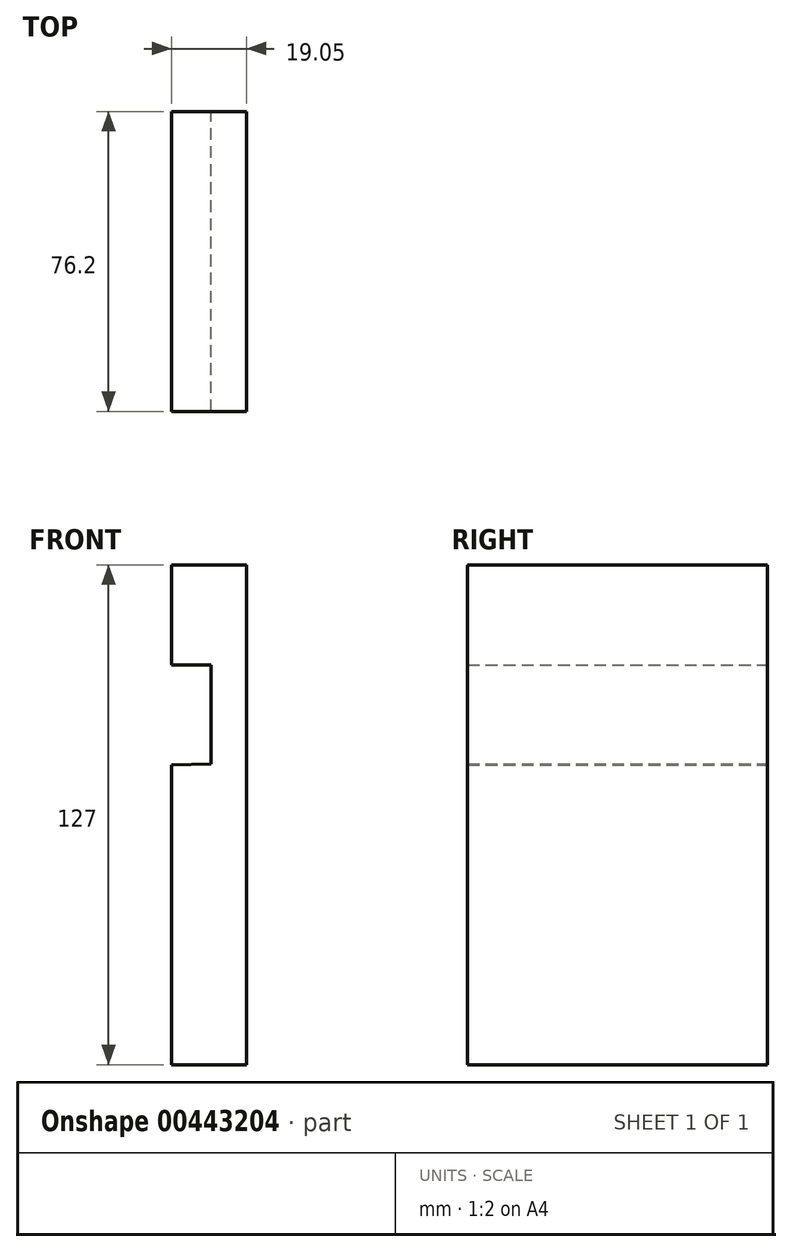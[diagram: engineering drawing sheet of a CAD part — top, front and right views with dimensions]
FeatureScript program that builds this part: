
annotation { "Feature Type Name" : "Feature", "Feature Type Description" : "" }
export const myFeature = defineFeature(function(context is Context, id is Id, definition is map)
    precondition{}
    {
        {
            var Q0;
            Q0=qCreatedBy(makeId("Front.planeOp"),FACE);
            var sketch = newSketch(context, id + "F0", { "sketchPlane" : qUnion([Q0])});
            skLineSegment(sketch, "E0", {"start": v(-2.9, 60.4) * mm, "end": v(-2.9, -66.6) * mm});
            skLineSegment(sketch, "E1", {"start": v(-2.9, -66.6) * mm, "end": v(-21.94, -66.6) * mm});
            skLineSegment(sketch, "E2", {"start": v(-2.9, 60.4) * mm, "end": v(-21.94, 60.4) * mm});
            skLineSegment(sketch, "E3", {"start": v(-21.94, 60.4) * mm, "end": v(-21.94, 35) * mm});
            skLineSegment(sketch, "E4", {"start": v(-21.94, 35) * mm, "end": v(-11.96, 35) * mm});
            skLineSegment(sketch, "E5", {"start": v(-11.96, 35) * mm, "end": v(-11.96, 9.85) * mm});
            skLineSegment(sketch, "E6", {"start": v(-21.94, -66.6) * mm, "end": v(-21.94, 9.6) * mm});
            skLineSegment(sketch, "E7", {"start": v(-21.94, 9.6) * mm, "end": v(-11.96, 9.85) * mm});
            skSolve(sketch);
        }
        {
            var Q0;
            Q0 = qSketchRegion(id + "F0", true);
            extrude(context, id + "F1", {"entities" : qUnion([Q0]), "depth" : 76.2 * mm});
        }
    });
